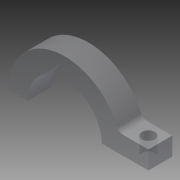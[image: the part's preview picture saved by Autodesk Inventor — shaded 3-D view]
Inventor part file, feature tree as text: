
AUTODESK INVENTOR PART (.ipt)
format: ipt  version: 2013 (Build 170138000, 138)  size: 97,792 bytes
history: native  units: in
note: dims shown in document units (in); Inventor stores cm internally (conversion verified against a paired STEP export)
features: sketch x2, extrude x1, fillet x1, hole x1
ambient origin geometry x8: Origin, YZ Plane, XZ Plane, XY Plane, X Axis, Y Axis, Z Axis, Center Point
bodies: Solid1 (feature_tree)
feature tree (5):
  extrude  "Extrusion1"  Depth=2.38in
  fillet  "Fillet1"  Radius=1.75in
  hole  "Hole1"  [1 undecoded]
  sketch  "Sketch1"  dims[d0=1.55in d1=2.38in d2=1.75in]
  sketch  "Sketch2"  dims[d3=0.5in d4=0.0in d5=0.125in d6=0.25in d7=0.25in d8=0.27in d9=0.75in d10=0.375in d11=0.25in d12=0.5635in d13=1.0in d14=0.8108in d15=0.38in]
note: 1 required parameter value undecoded (feature->parameter linkage not recoverable at this tier; creation-order binding heuristic only, values carry confidence <= 0.55)
